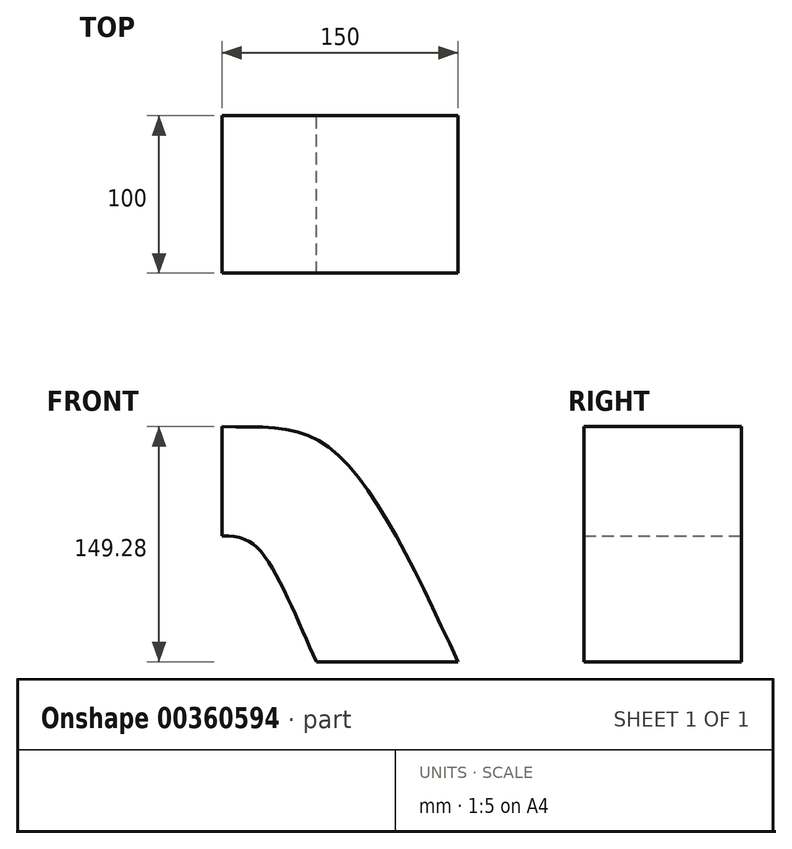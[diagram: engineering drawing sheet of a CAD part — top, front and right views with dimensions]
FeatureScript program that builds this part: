
annotation { "Feature Type Name" : "Feature", "Feature Type Description" : "" }
export const myFeature = defineFeature(function(context is Context, id is Id, definition is map)
    precondition{}
    {
        {
            var Q0;
            Q0=qCreatedBy(makeId("Front.planeOp"),FACE);
            var sketch = newSketch(context, id + "F0", { "sketchPlane" : qUnion([Q0])});
            skLineSegment(sketch, "E0", {"start": v(-57.45, 16.23) * mm, "end": v(-57.45, 85.51) * mm});
            skFitSpline(sketch, "E1", {"points": [v(-57.45, 16.23) * mm, v(-30.64, 3.48) * mm, v(2.55, -63.77) * mm], "startDerivative": vector(99.68, 0) * mm, "endDerivative": vector(46.73, -100.28) * mm});
            skFitSpline(sketch, "E2", {"points": [v(-57.45, 85.51) * mm, v(11.67, 71.61) * mm, v(92.55, -63.77) * mm], "startDerivative": vector(216.08, -1.73) * mm, "endDerivative": vector(120.9, -256.94) * mm});
            skLineSegment(sketch, "E3", {"start": v(2.55, -63.77) * mm, "end": v(92.55, -63.77) * mm});
            skSolve(sketch);
        }
        {
            var Q0;
            Q0 = qSketchRegion(id + "F0", true);
            extrude(context, id + "F1", {"entities" : qUnion([Q0]), "depth" : 100 * mm});
        }
    });
